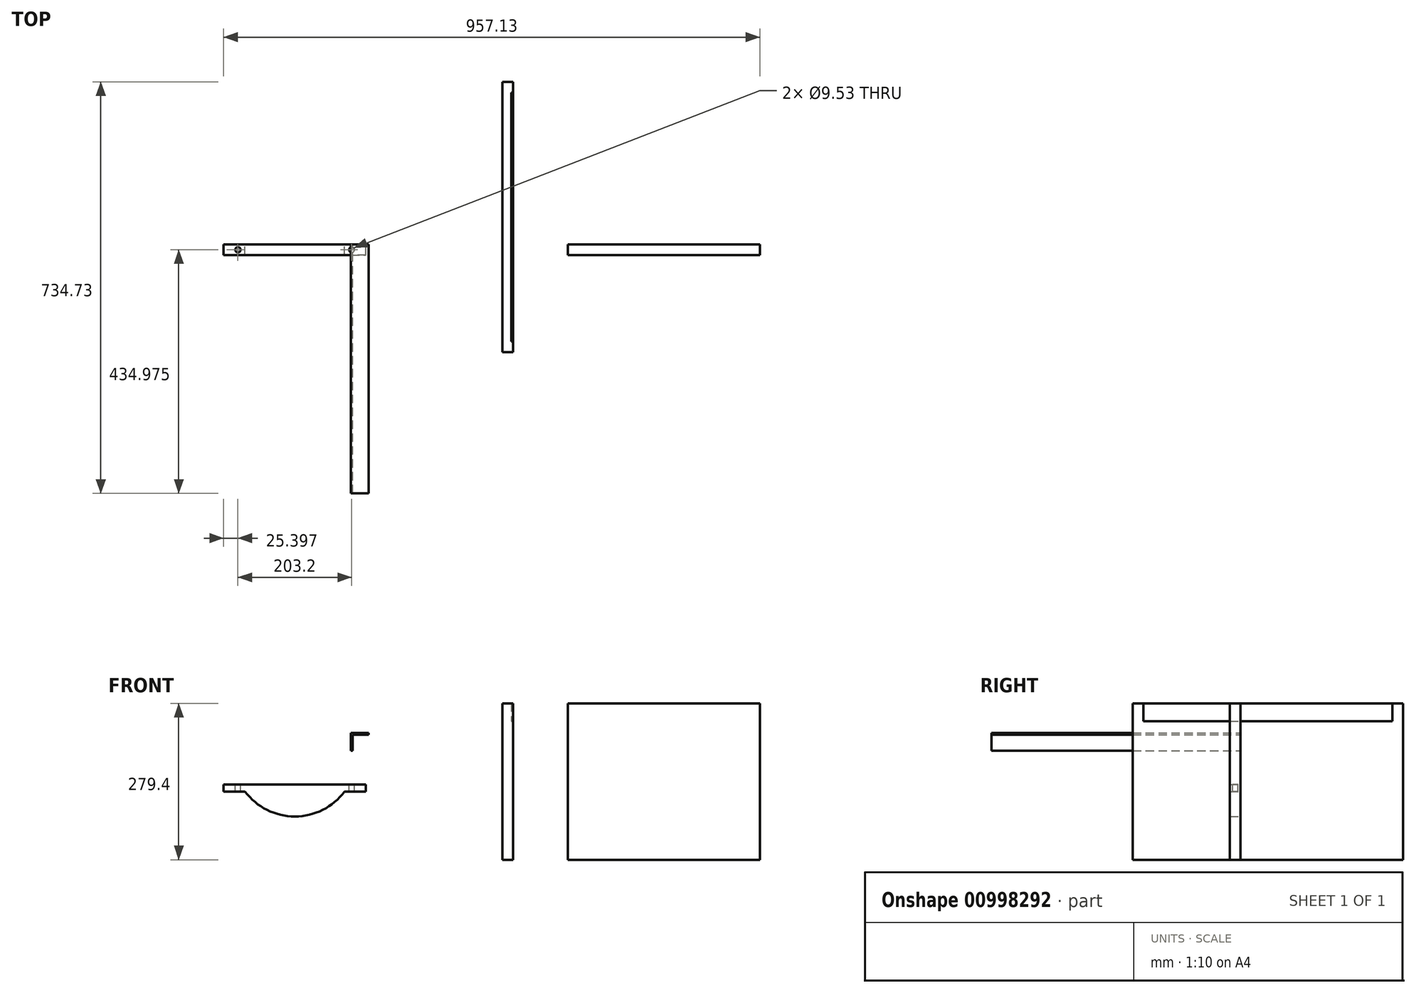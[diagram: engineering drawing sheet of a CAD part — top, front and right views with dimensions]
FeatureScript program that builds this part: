
annotation { "Feature Type Name" : "Feature", "Feature Type Description" : "" }
export const myFeature = defineFeature(function(context is Context, id is Id, definition is map)
    precondition{}
    {
        {
            var Q0;
            Q0=qCreatedBy(makeId("Right.planeOp"),FACE);
            var sketch = newSketch(context, id + "F0", { "sketchPlane" : qUnion([Q0])});
            skLineSegment(sketch, "E0.bottom", {"start": v(-192.37, 157.63) * mm, "end": v(290.23, 157.63) * mm});
            skLineSegment(sketch, "E0.top", {"start": v(-192.37, -121.77) * mm, "end": v(290.23, -121.77) * mm});
            skLineSegment(sketch, "E0.left", {"start": v(-192.37, 157.63) * mm, "end": v(-192.37, -121.77) * mm});
            skLineSegment(sketch, "E0.right", {"start": v(290.23, 157.63) * mm, "end": v(290.23, -121.77) * mm});
            skSolve(sketch);
        }
        {
            var Q0;
            Q0 = qSketchRegion(id + "F0", true);
            extrude(context, id + "F1", {"entities" : qUnion([Q0]), "depth" : 19.05 * mm, "offsetDistance" : 25.4 * mm});
        }
        {
            var Q0;
            Q0=qCreatedBy(makeId("Front.planeOp"),FACE);
            var sketch = newSketch(context, id + "F2", { "sketchPlane" : qUnion([Q0])});
            skLineSegment(sketch, "E1.bottom", {"start": v(116.86, 157.63) * mm, "end": v(459.76, 157.63) * mm});
            skLineSegment(sketch, "E1.top", {"start": v(116.86, -121.77) * mm, "end": v(459.76, -121.77) * mm});
            skLineSegment(sketch, "E1.left", {"start": v(116.86, 157.63) * mm, "end": v(116.86, -121.77) * mm});
            skLineSegment(sketch, "E1.right", {"start": v(459.76, 157.63) * mm, "end": v(459.76, -121.77) * mm});
            skSolve(sketch);
        }
        {
            var Q0;
            Q0 = qSketchRegion(id + "F2", true);
            extrude(context, id + "F3", {"entities" : qUnion([Q0]), "depth" : 19.05 * mm, "offsetDistance" : 25.4 * mm});
        }
        {
            var Q0;
            Q0=qCreatedBy(makeId("Front.planeOp"),FACE);
            var sketch = newSketch(context, id + "F4", { "sketchPlane" : qUnion([Q0])});
            skLineSegment(sketch, "E2", {"start": v(-267.12, 73.04) * mm, "end": v(-267.12, 101.62) * mm});
            skLineSegment(sketch, "E3", {"start": v(-267.12, 101.62) * mm, "end": v(-238.54, 101.62) * mm});
            skLineSegment(sketch, "E4", {"start": v(-238.54, 104.8) * mm, "end": v(-238.54, 101.62) * mm});
            skLineSegment(sketch, "E5", {"start": v(-238.54, 104.8) * mm, "end": v(-270.3, 104.8) * mm});
            skLineSegment(sketch, "E6", {"start": v(-270.3, 104.8) * mm, "end": v(-270.3, 73.04) * mm});
            skLineSegment(sketch, "E7", {"start": v(-267.12, 73.04) * mm, "end": v(-270.3, 73.04) * mm});
            skSolve(sketch);
        }
        {
            var Q0;
            Q0 = qSketchRegion(id + "F4", true);
            extrude(context, id + "F5", {"entities" : qUnion([Q0]), "depth" : 444.5 * mm, "offsetDistance" : 25.4 * mm});
        }
        {
            var Q0;
            Q0=makeQuery(id+"F1.opExtrude","CAP_FACE",FACE,{"disambiguationData":[OSD([sQuery(id+"F0.wireOp",EDGE,"E0.bottom"),sQuery(id+"F0.wireOp",EDGE,"E0.top"),sQuery(id+"F0.wireOp",EDGE,"E0.left"),sQuery(id+"F0.wireOp",EDGE,"E0.right")])],"isStart":false});
            var sketch = newSketch(context, id + "F6", { "sketchPlane" : qUnion([Q0])});
            skLineSegment(sketch, "E8", {"start": v(-173.32, 157.63) * mm, "end": v(-173.32, 125.88) * mm});
            skLineSegment(sketch, "E9", {"start": v(-173.32, 125.88) * mm, "end": v(271.18, 125.88) * mm});
            skLineSegment(sketch, "E10", {"start": v(271.18, 125.88) * mm, "end": v(271.18, 157.63) * mm});
            skLineSegment(sketch, "E11", {"start": v(-173.32, 157.63) * mm, "end": v(271.18, 157.63) * mm});
            skSolve(sketch);
        }
        {
            var Q0;
            Q0 = qSketchRegion(id + "F6", true);
            extrude(context, id + "F7", {"entities" : qUnion([Q0]), "operationType" : NewBodyOperationType.REMOVE, "oppositeDirection" : true, "depth" : 3.17 * mm, "offsetDistance" : 25.4 * mm});
        }
        {
            var Q0;
            Q0=qCreatedBy(makeId("Front.planeOp"),FACE);
            var sketch = newSketch(context, id + "F8", { "sketchPlane" : qUnion([Q0])});
            skLineSegment(sketch, "E12", {"start": v(-497.37, 12.7) * mm, "end": v(-243.37, 12.7) * mm});
            skLineSegment(sketch, "E13", {"start": v(-243.37, 12.7) * mm, "end": v(-243.37, 0) * mm});
            skLineSegment(sketch, "E14", {"start": v(-243.37, 0) * mm, "end": v(-281.47, 0) * mm});
            skLineSegment(sketch, "E15", {"start": v(-497.37, 12.7) * mm, "end": v(-497.37, 0) * mm});
            skLineSegment(sketch, "E16", {"start": v(-497.37, 0) * mm, "end": v(-459.27, 0) * mm});
            skLineSegment(sketch, "E17", {"start": v(-370.37, 39) * mm, "end": v(-370.37, -35.67) * mm, "construction": true});
            skArc(sketch, "E18", {"start": v(-459.27, 0) * mm, "mid": v(-370.37, -44.45) * mm, "end": v(-281.47, 0) * mm});
            skSolve(sketch);
        }
        {
            var Q0;
            Q0 = qSketchRegion(id + "F8", true);
            extrude(context, id + "F9", {"entities" : qUnion([Q0]), "depth" : 19.05 * mm, "offsetDistance" : 25.4 * mm});
        }
        {
            var Q0;
            Q0=makeQuery(id+"F9.opExtrude","SWEPT_FACE",FACE,{"disambiguationData":[OSD([sQuery(id+"F8.wireOp",EDGE,"E12")])]});
            var sketch = newSketch(context, id + "F10", { "sketchPlane" : qUnion([Q0])});
            skCircle(sketch, "E19", {"center": v(-471.97, -9.53) * mm, "radius": 4.76 * mm});
            skCircle(sketch, "E20", {"center": v(-268.77, -9.53) * mm, "radius": 4.76 * mm});
            skLineSegment(sketch, "E21", {"start": v(-497.37, -9.53) * mm, "end": v(-243.37, -9.53) * mm, "construction": true});
            skLineSegment(sketch, "E22", {"start": v(-370.37, 27.62) * mm, "end": v(-370.37, -53.23) * mm, "construction": true});
            skSolve(sketch);
        }
        {
            var Q0;
            Q0 = qSketchRegion(id + "F10", true);
            extrude(context, id + "F11", {"entities" : qUnion([Q0]), "operationType" : NewBodyOperationType.REMOVE, "endBound" : BoundingType.THROUGH_ALL, "oppositeDirection" : true, "depth" : 25.4 * mm, "offsetDistance" : 25.4 * mm});
        }
    });
